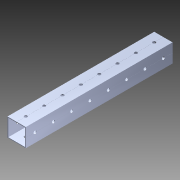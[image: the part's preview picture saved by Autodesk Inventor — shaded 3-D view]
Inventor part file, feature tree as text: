
AUTODESK INVENTOR PART (.ipt)
format: ipt  version: 2014 SP1 (Build 180222100, 222)  size: 1,105,408 bytes
history: native  units: in
note: dims shown in document units (in); Inventor stores cm internally (conversion verified against a paired STEP export)
features: pattern_circular x1, other x1, extrude x1, imported_body x1, sketch x1
ambient origin geometry x8: Origin, YZ Plane, XZ Plane, XY Plane, X Axis, Y Axis, Z Axis, Center Point
bodies: Body1 (feature_tree)
feature tree (5):
  pattern_circular  "CirPattern2"
  other  "1x1 tube1"
  extrude  "Extrusion1"  [1 undecoded]
  imported_body  "Base1"
  sketch  "Sketch1"  dims[d0=51.0in d1=0.0in]
note: 1 required parameter value undecoded (feature->parameter linkage not recoverable at this tier; creation-order binding heuristic only, values carry confidence <= 0.55)
